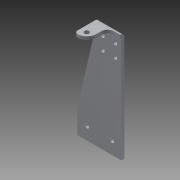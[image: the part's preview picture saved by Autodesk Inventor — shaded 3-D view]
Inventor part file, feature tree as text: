
AUTODESK INVENTOR PART (.ipt)
format: ipt  version: 2014 SP1 (Build 180222100, 222)  size: 175,104 bytes
history: native  units: in
note: dims shown in document units (in); Inventor stores cm internally (conversion verified against a paired STEP export)
features: other x3, sheet_metal_op x1, fillet x1, sketch x1
ambient origin geometry x8: Origin, YZ Plane, XZ Plane, XY Plane, X Axis, Y Axis, Z Axis, Center Point
bodies: Solid1 (feature_tree)
feature tree (6):
  sheet_metal_op  "Face1"
  fillet  "Fillet5"  Radius=4.1875in
  sketch  "Sketch1"  dims[d2=0.163in d4=0.7874in d6=1.0in d7=0.3937in d9=1.0in d11=0.0625in d22=0.5in d50=1.0in d51=1.75in d52=1.0in d53=0.375in d56=0.163in d57=0.25in d58=0.25in d59=0.7874in d61=0.5in d62=0.7874in d64=0.5in d67=0.125in d3=0.0625in]
  other  "Plate1"
  other  "Definition1"
  other  "Cut1"
